# Revit family: 02 BE 74.43
name_source: partatom
category: Plumbing Fixtures
revit_build: Autodesk Revit 2017 (Build: 20160225_1515(x64)
units: mm (PartAtom-declared; Revit-internal decimal feet)

## family parameters
Cut with Voids When Loaded = Yes
Host = Face
Part Type = Normal
Room Calculation Point = No
Round Connector Dimension = Use Diameter
Shared = No

## types (1)
- BE 74.43
    Acabado _lavaplato = Teka_Acero Inoxidable
    Ancho = 430 mm
    Ca_1_Accesorios = Válvula 3 1/2'' + Rebalse redondo. + Sifón y Completo sistema de conexión
    Ca_1_Dimensiones Lavaplatos = 787 x 482 mm
    Ca_1_Dimesiones Cubeta = 736 x 431 x 200 mm
    Ca_1_Espesor de acero = 0.8mm
    Ca_1_Instalación = Bajo encimera
    Ca_1_Material Principal = Acero Inoxidable AISI-304 (18/10)
    Ca_1_Profundidad Cubeta = 200 mm.
    Ca_1_Sello CE = Producto cumple Norma Europea EN-13310
    Ca_Certificaciones = Norma Europea EN-13310
    Ca_Creado por = Catálogo Arquitectura
    Ca_Código Catálogo Arquitectura = 411_Tek_044
    Ca_Código EAN = 8421152060889
    Ca_Código del Producto = 10125121
    Ca_Especificaciones Técnicas = Lavaplatos empotrable de acero TEKA modelo BE 74.43
    Ca_Fabricante = Teka
    Ca_Instalación = Bajo Encimera
    Ca_Itemizado CDT = E 04 05 01
    Ca_Masterformat = 22 41 16
    Ca_Material Principal = Acero Inoxidable AISI-304 (18/10)
    Ca_País de Fabricación = España
    Ca_Producto = Lavaplatos BE 74.43
    Ca_Representante = Teka
    Ca_Teléfono = 99821 1017
    Ca_Usos = Lavaplatos bajo encimera para cocina
    Ca_Web del Fabricante = www.teka.com
    Ca_Web del Representante = www.teka.cl
    Default Elevation = 1219 mm
    Description = Lavaplatos bajo encimera para cocina
    Espesor_Cubierta = 20 mm  [stored 0.0656168 ft]
    Largo = 735 mm  [stored 2.41142 ft]
    Manufacturer = Teka
    Model = BE 74.43
    URL = www.teka.cl
    Waste Connection = Yes

note: [stored X ft] marks values corroborated as IEEE doubles in the binary element streams (Revit-internal decimal feet)

## geometry (parser evidence)
native form markers: Sweep x2
no freeform markers — native parametric forms only
